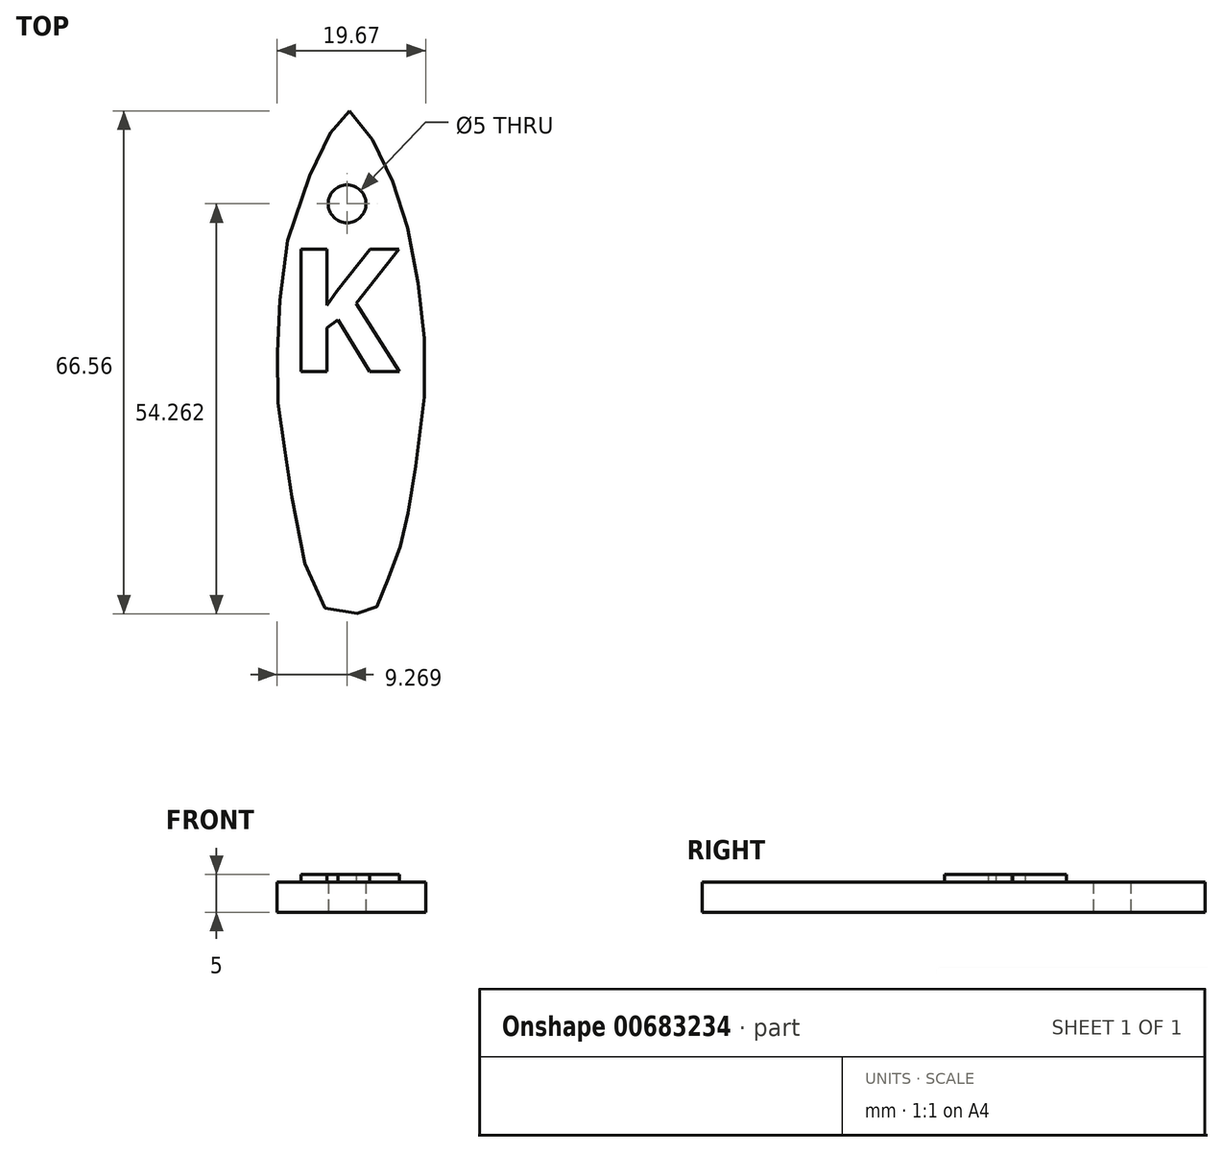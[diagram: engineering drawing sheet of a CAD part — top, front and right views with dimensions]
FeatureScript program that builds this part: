
annotation { "Feature Type Name" : "Feature", "Feature Type Description" : "" }
export const myFeature = defineFeature(function(context is Context, id is Id, definition is map)
    precondition{}
    {
        {
            var Q0;
            Q0=qCreatedBy(makeId("Top.planeOp"),FACE);
            var sketch = newSketch(context, id + "F0", { "sketchPlane" : qUnion([Q0])});
            skFitSpline(sketch, "E0", {"points": [v(-33.6, 66.47) * mm, v(-30.95, 63.4) * mm, v(-27.99, 57.35) * mm, v(-25.68, 50.1) * mm, v(-24.03, 39.76) * mm, v(-23.6, 29.87) * mm, v(-25.35, 16.14) * mm, v(-26.12, 11.85) * mm, v(-27.1, 8.11) * mm, v(-28.43, 4.7) * mm, v(-29.42, 1.96) * mm, v(-30.74, 0) * mm, v(-31.94, 0) * mm, v(-35.35, 0) * mm, v(-38.1, 2.4) * mm, v(-41.18, 15.04) * mm, v(-42.27, 22.4) * mm, v(-43.15, 29.76) * mm, v(-42.93, 38) * mm, v(-42.05, 48.22) * mm, v(-37.55, 60.86) * mm, v(-35.35, 64.82) * mm, v(-33.6, 66.47) * mm]});
            skCircle(sketch, "E1", {"center": v(-33.91, 54.17) * mm, "radius": 2.5 * mm});
            skText(sketch, "E2", { "text": "K", "fontName": "OpenSans-Bold.ttf"});
            const initialGuessF0  = {"E2": [-0.04204, 0.032, 1, 0, 0.0163]};
            skSetInitialGuess(sketch, initialGuessF0);
            skSolve(sketch);
        }
        {
            var Q0;
            Q0=makeQuery(id+"F0.imprint","IMPRINT",FACE,{"disambiguationData":[TD([[makeQuery(id+"F0.imprint","IMPRINT",EDGE,{"derivedFrom":sQuery(id+"F0.wireOp",EDGE,"E0")}),-1.0]])]});
            extrude(context, id + "F1", {"entities" : qUnion([Q0]), "depth" : 4 * mm, "offsetDistance" : 25.4 * mm});
        }
        {
            var Q0;
            Q0=makeQuery(id+"F0.imprint","IMPRINT",FACE,{"disambiguationData":[TD([[makeQuery(id+"F0.imprint","IMPRINT",EDGE,{"derivedFrom":sQuery(id+"F0.wireOp",EDGE,"E2.sketch_text.stroke-0")}),-1.0]])]});
            extrude(context, id + "F2", {"entities" : qUnion([Q0]), "operationType" : NewBodyOperationType.ADD, "depth" : 5 * mm, "offsetDistance" : 25 * mm});
        }
    });
